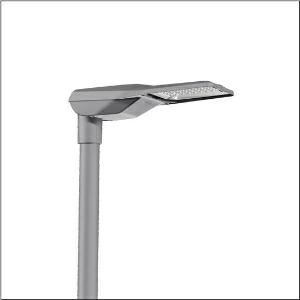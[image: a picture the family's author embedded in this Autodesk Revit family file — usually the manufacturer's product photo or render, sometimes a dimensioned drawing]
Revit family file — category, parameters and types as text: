
# Revit family: streetlight_sl_21_iq_mini___st0_5a_5xe2b41g08gb_465e
name_source: partatom
category: Lighting Fixtures
units: mm (PartAtom-declared; Revit-internal decimal feet)

## family parameters
Cut with Voids When Loaded = No
Host = Face
Light Source = No
Part Type = Normal
Room Calculation Point = No
Round Connector Dimension = Use Diameter
Shared = No

## types (1)
- --- (1 x LED, 5920 lm, 37.1 W, 4000K)
    Apparent Load = 37 VA
    CIE Flux Codes = 41 75 97 100 100
    Color Rendering = 70
    Color Temperature = 4000K
    Default Elevation = 1800 mm
    Description = Streetlight SL 21 iQ mini, mast luminaire, primary light control with lens, of PMMA, primary optical cover: cover, of toughened safety glass, transparent, light distribution: ST0.5a, light emission: direct distribution, primary light characteristic: asymmetric, installation type: post-top, side-entry, LED, High Power LED, rated luminous flux: 5.920lm, luminous efficacy: 160lm/W, light colour: 740, colour temperature: 4000K, control: Street-Remote, Auto-Match, Temp-Guard, Lumen-Switch, Night-Set, Smart-Wire, Light-Fading, Desk-Remote (wireless, voltage-free reading and setting of iQ features in the workshop via application-optimized NFC function/RFID function), optimised constant luminous flux control (CLO 2.0), presetting dimming linear, mains connection: 220..240V, AC, 50/60Hz, start of lifetime: 37W, end of service life: 39W, reduction: 18W, luminaire housing, of diecast aluminium, powder-coated, Siteco® metallic grey (DB 702S), corrosivity category C5 mid according to DIN EN ISO 12944, please order mast flange separately, inclination adjustable: 0°, 5°, 10°, 15°, sealing non-destructively replaceable, multi-level sealing system, length: 628mm, width: 235mm, height: 110mm, mast flange for spigot size: 42mm (side-entry): 5XC10008XM4, 60/48mm (side-entry/post-top): 5XC10108XM2, 76/60mm (side-entry/post-top): 5XC10108XM1, protection rating (complete): IP66, insulation class (complete): insulation class II (safety insulation), certification: CE, ENEC, ENEC+, VDE, impact resistance: IK09, permissible operating ambient temperature for outdoor applications: -40..+50°C, standard-compliant lighting for roads and squares, packaging unit: 1 piece

Light Distribution: ST0.5a
    Height = 110 mm
    Lamp = 1 x LED
    Lamp Light Flux = 5920 lm
    Lamp Power = 37.1 W
    Lamp count = 1
    Length = 625 mm
    Luminous efficacy = 160 lm/W
    Manufacturer = Siteco
    ModVariant = No
    Model = 5XE2B41G08GB
    Number of Poles = 1
    OnlyDefault = Yes
    Power Factor = 1
    Product Name = Streetlight SL 21 iQ mini | ST0.5a
    Product group = mast luminaire | pylon top
    ProductGroupID = 6100
    Protection Class = Protection class II
    Protection Degree = IP 66
    RLX_Detail_Level = 1
    RLX_Emergency_Light_Flux = 0 lm
    RLX_Emergency_Type = 0
    RLX_Emergency_Type_DB = No
    RlxData = <blob elided: 103177 chars, md5=a733504a>
    Socket = socket
    Standby Power = 0 W
    System Light Flux = 5920 lm
    System Power = 37 W
    Type Comments = factory setting: luminous flux: 100 % | dim-lin: 254 | 385 mA
    Type Image = l_1003519.jpg
    URL = http://relux.com
    VarID = @adj_125443
    Voltage = 0 V
    Weight = 0.00 kg
    Width = 234 mm

## geometry (parser evidence)
native form markers: Blend x4, Sweep x8
no freeform markers — native parametric forms only
